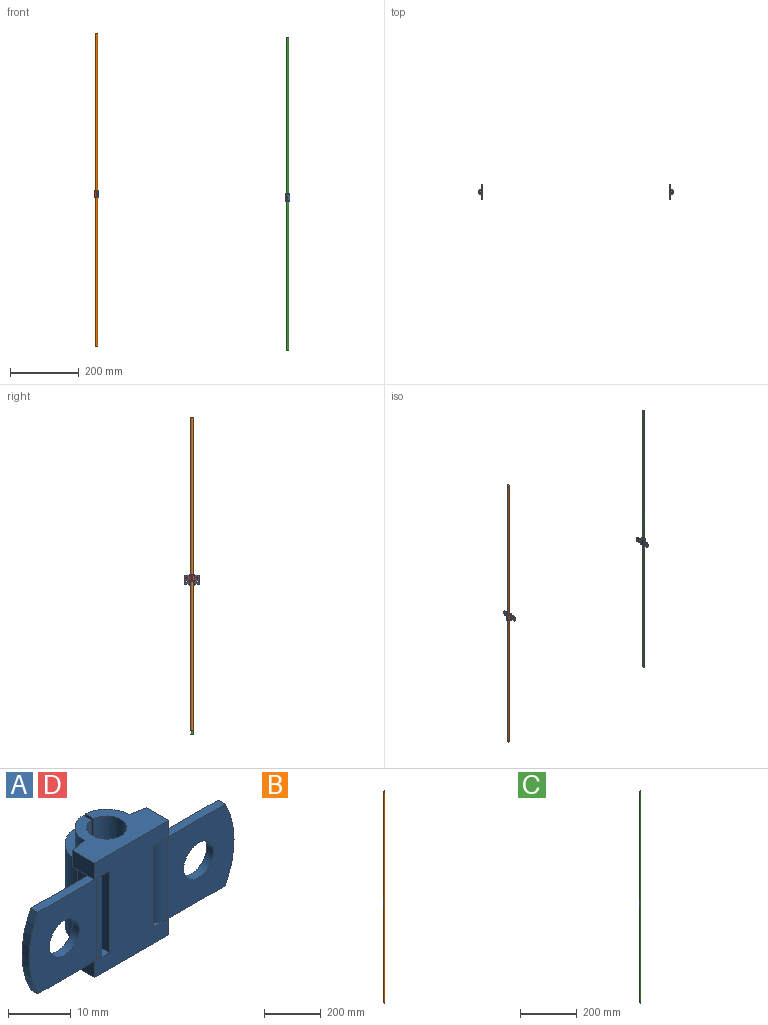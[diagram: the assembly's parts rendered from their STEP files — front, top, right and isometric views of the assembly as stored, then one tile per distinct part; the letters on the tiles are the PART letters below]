
ASSEMBLY  parts=4 mates=4
PART A: 48 faces, bbox 46x12.2x22.2 mm
  f0: cylinder r=5.02mm len=5.01mm, axis (0,0,-1), area 24.2mm2, adj f16,f23,f27,f29
  f1: cylinder r=5.02mm len=5.01mm, axis (0,0,-1), area 24.2mm2, adj f15,f23,f26,f29
  f2: plane 2.78x2.78mm, normal (0,0,-1), area 1.7mm2, adj f6,f13,f45
  f3: plane 3.72x1.71mm, normal (0,0,-1), area 5.8mm2, adj f16,f17,f38,f43,f44
  f4: plane 3.72x1.71mm, normal (0,0,1), area 5.8mm2, adj f19,f20,f38,f43,f44
  f5: plane 2.78x2.78mm, normal (0,0,1), area 1.7mm2, adj f6,f13,f45
  f6: plane 15.88x2.78mm, normal (-1,0,0), area 44.1mm2, adj f2,f5,f13,f45
  f7: plane 2.78x2.78mm, normal (0,0,-1), area 1.7mm2, adj f13,f25,f39
  f8: plane 3.72x1.71mm, normal (0,0,-1), area 5.8mm2, adj f14,f15,f37,f40,f41
  f9: plane 3.72x1.71mm, normal (0,0,1), area 5.8mm2, adj f21,f22,f37,f40,f41
  f10: plane 2.78x2.78mm, normal (0,0,1), area 1.7mm2, adj f13,f25,f39
  f11: cylinder r=3.17mm len=22.23mm, axis (0,0,-1), area 432.1mm2, adj f23,f24,f26,f27
  f12: cylinder r=5.02mm len=5.01mm, axis (0,0,-1), area 24.2mm2, adj f19,f24,f27,f33
  f13: plane 46.02x22.23mm, normal (0,-1,0), area 656mm2, adj f2,f5,f6,f7,f10,f14,f17,f20
  f14: plane 5.01x3.18mm, normal (1,0,0), area 15.9mm2, adj f8,f13,f15,f23,f31
  f15: plane 3.3x3.18mm, normal (0.17,0.98,0), area 10.6mm2, adj f1,f8,f14,f23,f29
  f16: plane 3.3x3.18mm, normal (-0.17,0.98,0), area 10.6mm2, adj f0,f3,f17,f23,f29
  f17: plane 5.01x3.18mm, normal (-1,0,0), area 15.9mm2, adj f3,f13,f16,f23,f30
  f18: cylinder r=5.02mm len=5.01mm, axis (0,0,-1), area 24.2mm2, adj f22,f24,f26,f33
  f19: plane 3.3x3.18mm, normal (-0.17,0.98,0), area 10.6mm2, adj f4,f12,f20,f24,f33
  f20: plane 5.01x3.18mm, normal (-1,0,0), area 15.9mm2, adj f4,f13,f19,f24,f32
  f21: plane 5.01x3.18mm, normal (1,0,0), area 15.9mm2, adj f9,f13,f22,f24,f34
  f22: plane 3.3x3.18mm, normal (0.17,0.98,0), area 10.6mm2, adj f9,f18,f21,f24,f33
  f23: plane 16.64x10.6mm, normal (0,0,1), area 98mm2, adj f0,f1,f11,f13,f14,f15,f16,f17
  f24: plane 16.64x10.6mm, normal (0,0,-1), area 98mm2, adj f11,f12,f13,f18,f19,f20,f21,f22
  f25: plane 15.88x2.78mm, normal (1,0,0), area 44.1mm2, adj f7,f10,f13,f39
  f26: plane 22.23x1.85mm, normal (-1,0,0), area 41mm2, adj f1,f11,f18,f23,f24,f28
  f27: plane 22.23x1.85mm, normal (1,0,0), area 41mm2, adj f0,f11,f12,f23,f24,f28
  f28: cylinder r=5.02mm len=15.88mm, axis (0,0,-1), area 8.1mm2, adj f26,f27,f29,f33
  f29: plane 13.21x6.88mm, normal (0,0,1), area 29.4mm2, adj f0,f1,f15,f16,f28,f41,f42,f43
  f30: plane 12.71x1.59mm, normal (0,0,1), area 20.2mm2, adj f13,f17,f38,f47
  f31: plane 12.71x1.59mm, normal (0,0,1), area 20.2mm2, adj f13,f14,f37,f46
  f32: plane 12.71x1.59mm, normal (0,0,-1), area 20.2mm2, adj f13,f20,f38,f47
  f33: plane 13.21x6.88mm, normal (0,0,-1), area 29.4mm2, adj f12,f18,f19,f22,f28,f41,f42,f43
  f34: plane 12.71x1.59mm, normal (0,0,-1), area 20.2mm2, adj f13,f21,f37,f46
  f35: cylinder r=3.37mm len=6.75mm, axis (0,-1,0), area 33.6mm2, adj f13,f37
  f36: cylinder r=3.37mm len=6.75mm, axis (0,-1,0), area 33.6mm2, adj f13,f38
  f37: plane 15.88x15.21mm, normal (0,1,0), area 195.5mm2, adj f8,f9,f31,f34,f35,f40,f46
  f38: plane 15.88x15.21mm, normal (0,1,0), area 195.5mm2, adj f3,f4,f30,f32,f36,f44,f47
  f39: cylinder r=2.78mm len=15.88mm, axis (0,0,-1), area 69.3mm2, adj f7,f10,f13,f25
  f40: cylinder r=1.19mm len=15.88mm, axis (0,0,-1), area 29.7mm2, adj f8,f9,f37,f41
  f41: plane 15.88x2.81mm, normal (1,0,0), area 44.6mm2, adj f8,f9,f29,f33,f40,f42
  f42: cylinder r=6.6mm len=15.88mm, axis (0,0,-1), area 329.4mm2, adj f29,f33,f41,f43
  f43: plane 15.88x2.81mm, normal (-1,0,0), area 44.6mm2, adj f3,f4,f29,f33,f42,f44
  f44: cylinder r=1.19mm len=15.88mm, axis (0,0,-1), area 29.7mm2, adj f3,f4,f38,f43
  f45: cylinder r=2.78mm len=15.88mm, axis (0,0,-1), area 69.3mm2, adj f2,f5,f6,f13
  f46: cylinder r=16.87mm len=15.88mm, axis (0,-1,0), area 26.2mm2, adj f13,f31,f34,f37
  f47: cylinder r=16.87mm len=15.88mm, axis (0,-1,0), area 26.2mm2, adj f13,f30,f32,f38
PART B: 3 faces, bbox 6.4x6.4x914.4 mm
  f0: cylinder r=3.17mm len=914.4mm, axis (0,0,-1), area 18241.5mm2, adj f1,f2
  f1: plane 6.35x6.35mm, normal (0,0,1), area 31.7mm2, adj f0
  f2: plane 6.35x6.35mm, normal (0,0,-1), area 31.7mm2, adj f0
PART C: 3 faces, bbox 6.4x6.4x914.4 mm
  f0: cylinder r=3.17mm len=914.4mm, axis (0,0,-1), area 18241.5mm2, adj f1,f2
  f1: plane 6.35x6.35mm, normal (0,0,1), area 31.7mm2, adj f0
  f2: plane 6.35x6.35mm, normal (0,0,-1), area 31.7mm2, adj f0
PART D: same geometry as A
PLACE A rot(axis=(0,0,-1),90deg) t=(552.7,0.51,-11.11)mm
PLACE B rot(axis=(0,0,1),90deg) t=(0.51,0.6,11.11)mm
PLACE C rot(axis=(0,0,-1),90deg) t=(558.29,559.31,0)mm
PLACE D rot(axis=(0,0,1),90deg) t=(6.1,0.6,0)mm
MATE slider A.f0 <-> C.f0  axis (0,0,1) through (558.29,0.51,0)mm
MATE revolute D.f0 <-> B.f0  axis (0,0,1) through (0.51,0.6,11.11)mm
MATE revolute A.f0 <-> C.f0  axis (0,0,1) through (558.29,0.51,0)mm
MATE slider D.f0 <-> B.f0  axis (0,0,1) through (0.51,0.6,11.11)mm
